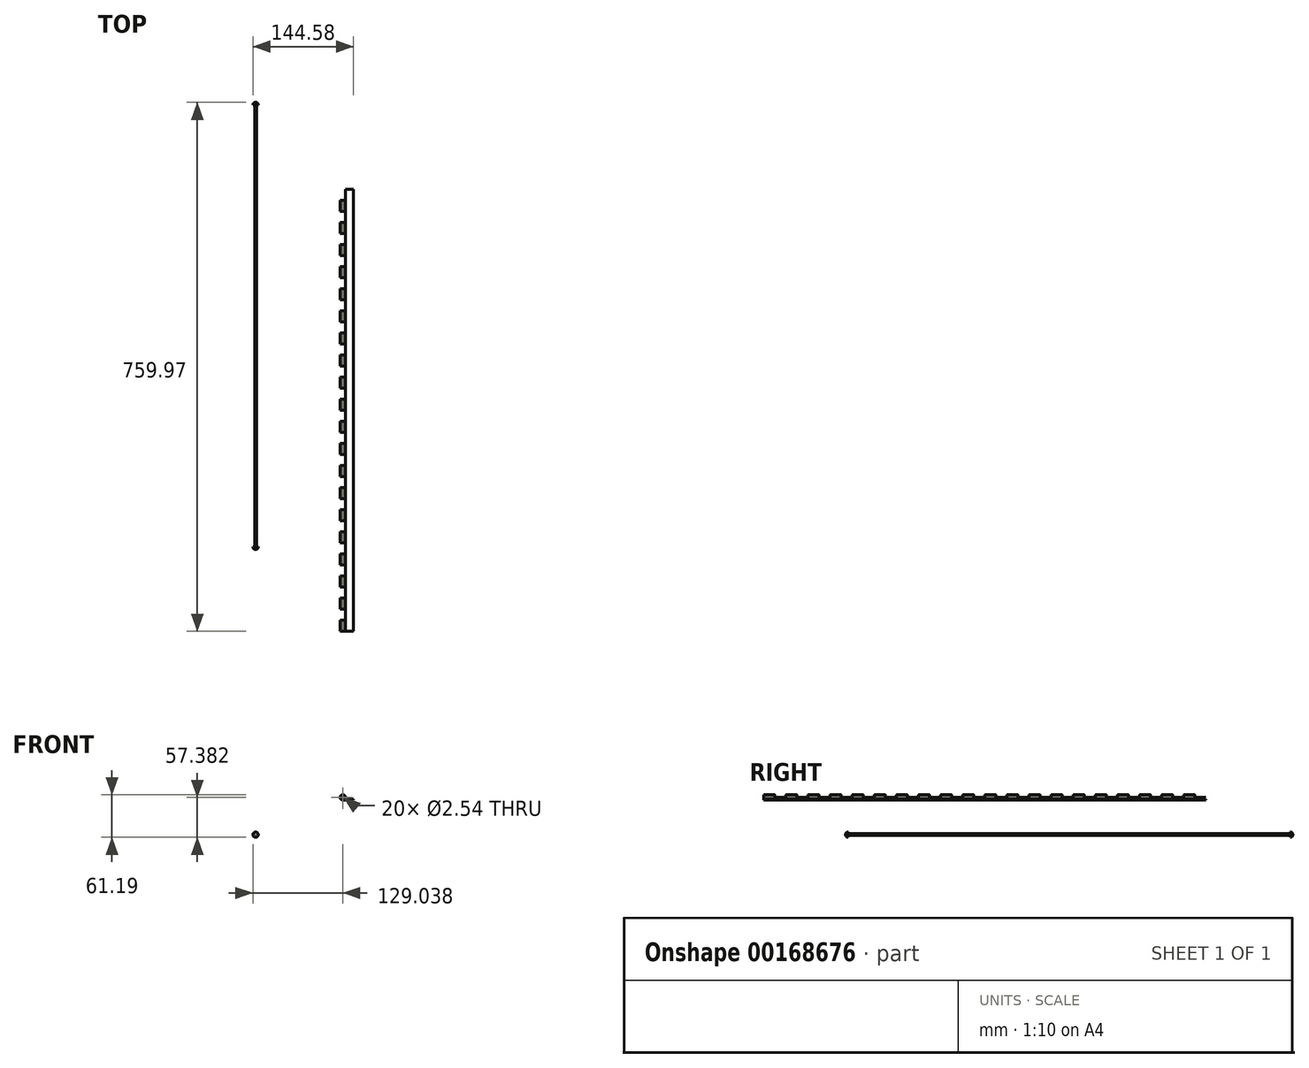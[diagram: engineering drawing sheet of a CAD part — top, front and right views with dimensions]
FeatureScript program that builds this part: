
annotation { "Feature Type Name" : "Feature", "Feature Type Description" : "" }
export const myFeature = defineFeature(function(context is Context, id is Id, definition is map)
    precondition{}
    {
        {
            var Q0;
            Q0=qCreatedBy(makeId("Front.planeOp"),FACE);
            var sketch = newSketch(context, id + "F0", { "sketchPlane" : qUnion([Q0])});
            skCircle(sketch, "E0", {"center": v(-17.02, 53.57) * mm, "radius": 3.81 * mm});
            skLineSegment(sketch, "E1", {"start": v(-17.02, 53.57) * mm, "end": v(-17.02, 20.01) * mm, "construction": true});
            skLineSegment(sketch, "E2", {"start": v(-17.02, 49.76) * mm, "end": v(-1.48, 49.76) * mm});
            skLineSegment(sketch, "E3", {"start": v(-1.48, 49.76) * mm, "end": v(-1.48, 51.03) * mm});
            skLineSegment(sketch, "E4", {"start": v(-1.48, 51.03) * mm, "end": v(-14.18, 51.03) * mm});
            skCircle(sketch, "E5", {"center": v(-17.02, 53.57) * mm, "radius": 1.27 * mm});
            skLineSegment(sketch, "E6", {"start": v(-14.18, 51.03) * mm, "end": v(-14.18, 67.2) * mm, "construction": true});
            skLineSegment(sketch, "E7", {"start": v(-17.02, 53.57) * mm, "end": v(18.39, 53.57) * mm});
            skPoint(sketch, "E8", {"position": v(-13.21, 53.57) * mm});
            skSolve(sketch);
        }
        {
            var Q0;
            Q0 = qSketchRegion(id + "F0", true);
            extrude(context, id + "F1", {"entities" : qUnion([Q0]), "depth" : 635 * mm});
        }
        {
            var Q0;
            Q0=qCreatedBy(makeId("Top.planeOp"),FACE);
            var sketch = newSketch(context, id + "F2", { "sketchPlane" : qUnion([Q0])});
            skLineSegment(sketch, "E9.bottom", {"start": v(-25.92, 0) * mm, "end": v(-13.22, 0) * mm});
            skLineSegment(sketch, "E9.top", {"start": v(-25.92, -15.87) * mm, "end": v(-13.22, -15.87) * mm});
            skLineSegment(sketch, "E9.left", {"start": v(-25.92, 0) * mm, "end": v(-25.92, -15.87) * mm});
            skLineSegment(sketch, "E9.right", {"start": v(-13.22, 0) * mm, "end": v(-13.22, -15.87) * mm});
            skLineSegment(sketch, "E10.0.1.0", {"start": v(-25.92, -31.75) * mm, "end": v(-25.92, -47.62) * mm});
            skLineSegment(sketch, "E10.0.1.1", {"start": v(-25.92, -31.75) * mm, "end": v(-13.22, -31.75) * mm});
            skLineSegment(sketch, "E10.0.1.2", {"start": v(-25.92, -47.62) * mm, "end": v(-13.22, -47.62) * mm});
            skLineSegment(sketch, "E10.0.1.3", {"start": v(-13.22, -31.75) * mm, "end": v(-13.22, -47.62) * mm});
            skLineSegment(sketch, "E10.0.2.0", {"start": v(-25.92, -63.5) * mm, "end": v(-25.92, -79.37) * mm});
            skLineSegment(sketch, "E10.0.2.1", {"start": v(-25.92, -63.5) * mm, "end": v(-13.22, -63.5) * mm});
            skLineSegment(sketch, "E10.0.2.2", {"start": v(-25.92, -79.38) * mm, "end": v(-13.22, -79.38) * mm});
            skLineSegment(sketch, "E10.0.2.3", {"start": v(-13.22, -63.5) * mm, "end": v(-13.22, -79.37) * mm});
            skLineSegment(sketch, "E10.0.3.0", {"start": v(-25.92, -95.25) * mm, "end": v(-25.92, -111.12) * mm});
            skLineSegment(sketch, "E10.0.3.1", {"start": v(-25.92, -95.25) * mm, "end": v(-13.22, -95.25) * mm});
            skLineSegment(sketch, "E10.0.3.2", {"start": v(-25.92, -111.12) * mm, "end": v(-13.22, -111.12) * mm});
            skLineSegment(sketch, "E10.0.3.3", {"start": v(-13.22, -95.25) * mm, "end": v(-13.22, -111.12) * mm});
            skLineSegment(sketch, "E10.0.4.0", {"start": v(-25.92, -127) * mm, "end": v(-25.92, -142.87) * mm});
            skLineSegment(sketch, "E10.0.4.1", {"start": v(-25.92, -127) * mm, "end": v(-13.22, -127) * mm});
            skLineSegment(sketch, "E10.0.4.2", {"start": v(-25.92, -142.88) * mm, "end": v(-13.22, -142.88) * mm});
            skLineSegment(sketch, "E10.0.4.3", {"start": v(-13.22, -127) * mm, "end": v(-13.22, -142.87) * mm});
            skLineSegment(sketch, "E10.0.5.0", {"start": v(-25.92, -158.75) * mm, "end": v(-25.92, -174.62) * mm});
            skLineSegment(sketch, "E10.0.5.1", {"start": v(-25.92, -158.75) * mm, "end": v(-13.22, -158.75) * mm});
            skLineSegment(sketch, "E10.0.5.2", {"start": v(-25.92, -174.62) * mm, "end": v(-13.22, -174.62) * mm});
            skLineSegment(sketch, "E10.0.5.3", {"start": v(-13.22, -158.75) * mm, "end": v(-13.22, -174.62) * mm});
            skLineSegment(sketch, "E10.0.6.0", {"start": v(-25.92, -190.5) * mm, "end": v(-25.92, -206.37) * mm});
            skLineSegment(sketch, "E10.0.6.1", {"start": v(-25.92, -190.5) * mm, "end": v(-13.22, -190.5) * mm});
            skLineSegment(sketch, "E10.0.6.2", {"start": v(-25.92, -206.38) * mm, "end": v(-13.22, -206.38) * mm});
            skLineSegment(sketch, "E10.0.6.3", {"start": v(-13.22, -190.5) * mm, "end": v(-13.22, -206.37) * mm});
            skLineSegment(sketch, "E10.0.7.0", {"start": v(-25.92, -222.25) * mm, "end": v(-25.92, -238.12) * mm});
            skLineSegment(sketch, "E10.0.7.1", {"start": v(-25.92, -222.25) * mm, "end": v(-13.22, -222.25) * mm});
            skLineSegment(sketch, "E10.0.7.2", {"start": v(-25.92, -238.12) * mm, "end": v(-13.22, -238.12) * mm});
            skLineSegment(sketch, "E10.0.7.3", {"start": v(-13.22, -222.25) * mm, "end": v(-13.22, -238.12) * mm});
            skLineSegment(sketch, "E10.0.8.0", {"start": v(-25.92, -254) * mm, "end": v(-25.92, -269.87) * mm});
            skLineSegment(sketch, "E10.0.8.1", {"start": v(-25.92, -254) * mm, "end": v(-13.22, -254) * mm});
            skLineSegment(sketch, "E10.0.8.2", {"start": v(-25.92, -269.88) * mm, "end": v(-13.22, -269.88) * mm});
            skLineSegment(sketch, "E10.0.8.3", {"start": v(-13.22, -254) * mm, "end": v(-13.22, -269.87) * mm});
            skLineSegment(sketch, "E10.0.9.0", {"start": v(-25.92, -285.75) * mm, "end": v(-25.92, -301.62) * mm});
            skLineSegment(sketch, "E10.0.9.1", {"start": v(-25.92, -285.75) * mm, "end": v(-13.22, -285.75) * mm});
            skLineSegment(sketch, "E10.0.9.2", {"start": v(-25.92, -301.62) * mm, "end": v(-13.22, -301.62) * mm});
            skLineSegment(sketch, "E10.0.9.3", {"start": v(-13.22, -285.75) * mm, "end": v(-13.22, -301.62) * mm});
            skLineSegment(sketch, "E10.0.10.0", {"start": v(-25.92, -317.5) * mm, "end": v(-25.92, -333.37) * mm});
            skLineSegment(sketch, "E10.0.10.1", {"start": v(-25.92, -317.5) * mm, "end": v(-13.22, -317.5) * mm});
            skLineSegment(sketch, "E10.0.10.2", {"start": v(-25.92, -333.38) * mm, "end": v(-13.22, -333.38) * mm});
            skLineSegment(sketch, "E10.0.10.3", {"start": v(-13.22, -317.5) * mm, "end": v(-13.22, -333.37) * mm});
            skLineSegment(sketch, "E10.0.11.0", {"start": v(-25.92, -349.25) * mm, "end": v(-25.92, -365.12) * mm});
            skLineSegment(sketch, "E10.0.11.1", {"start": v(-25.92, -349.25) * mm, "end": v(-13.22, -349.25) * mm});
            skLineSegment(sketch, "E10.0.11.2", {"start": v(-25.92, -365.12) * mm, "end": v(-13.22, -365.12) * mm});
            skLineSegment(sketch, "E10.0.11.3", {"start": v(-13.22, -349.25) * mm, "end": v(-13.22, -365.12) * mm});
            skLineSegment(sketch, "E10.direction1", {"start": v(-25.92, -15.87) * mm, "end": v(102.36, -15.87) * mm, "construction": true});
            skLineSegment(sketch, "E10.direction2", {"start": v(-25.92, -15.88) * mm, "end": v(-25.92, -47.62) * mm, "construction": true});
            skLineSegment(sketch, "E11.0.0.12", {"start": v(-25.92, -381) * mm, "end": v(-25.92, -396.87) * mm});
            skLineSegment(sketch, "E11.3.0.12", {"start": v(-25.92, -381) * mm, "end": v(-13.22, -381) * mm});
            skLineSegment(sketch, "E11.6.0.12", {"start": v(-25.92, -396.88) * mm, "end": v(-13.22, -396.88) * mm});
            skLineSegment(sketch, "E11.9.0.12", {"start": v(-13.22, -381) * mm, "end": v(-13.22, -396.87) * mm});
            skLineSegment(sketch, "E12.0.0.13", {"start": v(-25.92, -412.75) * mm, "end": v(-25.92, -428.62) * mm});
            skLineSegment(sketch, "E12.3.0.13", {"start": v(-25.92, -412.75) * mm, "end": v(-13.22, -412.75) * mm});
            skLineSegment(sketch, "E12.6.0.13", {"start": v(-25.92, -428.62) * mm, "end": v(-13.22, -428.62) * mm});
            skLineSegment(sketch, "E12.9.0.13", {"start": v(-13.22, -412.75) * mm, "end": v(-13.22, -428.62) * mm});
            skLineSegment(sketch, "E12.0.0.14", {"start": v(-25.92, -444.5) * mm, "end": v(-25.92, -460.37) * mm});
            skLineSegment(sketch, "E12.3.0.14", {"start": v(-25.92, -444.5) * mm, "end": v(-13.22, -444.5) * mm});
            skLineSegment(sketch, "E12.6.0.14", {"start": v(-25.92, -460.38) * mm, "end": v(-13.22, -460.38) * mm});
            skLineSegment(sketch, "E12.9.0.14", {"start": v(-13.22, -444.5) * mm, "end": v(-13.22, -460.37) * mm});
            skLineSegment(sketch, "E12.0.0.15", {"start": v(-25.92, -476.25) * mm, "end": v(-25.92, -492.12) * mm});
            skLineSegment(sketch, "E12.3.0.15", {"start": v(-25.92, -476.25) * mm, "end": v(-13.22, -476.25) * mm});
            skLineSegment(sketch, "E12.6.0.15", {"start": v(-25.92, -492.12) * mm, "end": v(-13.22, -492.12) * mm});
            skLineSegment(sketch, "E12.9.0.15", {"start": v(-13.22, -476.25) * mm, "end": v(-13.22, -492.12) * mm});
            skLineSegment(sketch, "E12.0.0.16", {"start": v(-25.92, -508) * mm, "end": v(-25.92, -523.87) * mm});
            skLineSegment(sketch, "E12.3.0.16", {"start": v(-25.92, -508) * mm, "end": v(-13.22, -508) * mm});
            skLineSegment(sketch, "E12.6.0.16", {"start": v(-25.92, -523.88) * mm, "end": v(-13.22, -523.88) * mm});
            skLineSegment(sketch, "E12.9.0.16", {"start": v(-13.22, -508) * mm, "end": v(-13.22, -523.87) * mm});
            skLineSegment(sketch, "E12.0.0.17", {"start": v(-25.92, -539.75) * mm, "end": v(-25.92, -555.62) * mm});
            skLineSegment(sketch, "E12.3.0.17", {"start": v(-25.92, -539.75) * mm, "end": v(-13.22, -539.75) * mm});
            skLineSegment(sketch, "E12.6.0.17", {"start": v(-25.92, -555.62) * mm, "end": v(-13.22, -555.62) * mm});
            skLineSegment(sketch, "E12.9.0.17", {"start": v(-13.22, -539.75) * mm, "end": v(-13.22, -555.62) * mm});
            skLineSegment(sketch, "E12.0.0.18", {"start": v(-25.92, -571.5) * mm, "end": v(-25.92, -587.37) * mm});
            skLineSegment(sketch, "E12.3.0.18", {"start": v(-25.92, -571.5) * mm, "end": v(-13.22, -571.5) * mm});
            skLineSegment(sketch, "E12.6.0.18", {"start": v(-25.92, -587.38) * mm, "end": v(-13.22, -587.38) * mm});
            skLineSegment(sketch, "E12.9.0.18", {"start": v(-13.22, -571.5) * mm, "end": v(-13.22, -587.37) * mm});
            skLineSegment(sketch, "E12.0.0.19", {"start": v(-25.92, -603.25) * mm, "end": v(-25.92, -619.12) * mm});
            skLineSegment(sketch, "E12.3.0.19", {"start": v(-25.92, -603.25) * mm, "end": v(-13.22, -603.25) * mm});
            skLineSegment(sketch, "E12.6.0.19", {"start": v(-25.92, -619.12) * mm, "end": v(-13.22, -619.12) * mm});
            skLineSegment(sketch, "E12.9.0.19", {"start": v(-13.22, -603.25) * mm, "end": v(-13.22, -619.12) * mm});
            skSolve(sketch);
        }
        {
            var Q0;
            Q0 = qSketchRegion(id + "F2", true);
            extrude(context, id + "F3", {"entities" : qUnion([Q0]), "operationType" : NewBodyOperationType.REMOVE, "depth" : 127 * mm});
        }
        {
            var Q0;
            Q0=qCreatedBy(makeId("Top.planeOp"),FACE);
            var sketch = newSketch(context, id + "F4", { "sketchPlane" : qUnion([Q0])});
            skLineSegment(sketch, "E13", {"start": v(-142.25, 121.16) * mm, "end": v(-140.98, 121.16) * mm});
            skLineSegment(sketch, "E14", {"start": v(-140.98, 121.16) * mm, "end": v(-140.98, -513.84) * mm});
            skLineSegment(sketch, "E15", {"start": v(-140.98, -513.84) * mm, "end": v(-142.25, -513.84) * mm});
            skLineSegment(sketch, "E16", {"start": v(-142.25, -513.84) * mm, "end": v(-142.25, 121.16) * mm});
            skLineSegment(sketch, "E17", {"start": v(-140.98, -513.84) * mm, "end": v(-138.44, -513.84) * mm});
            skArc(sketch, "E18", {"start": v(-138.44, -513.84) * mm, "mid": v(-139.56, -516.54) * mm, "end": v(-142.25, -517.65) * mm});
            skLineSegment(sketch, "E19", {"start": v(-142.25, -513.84) * mm, "end": v(-142.25, -517.65) * mm});
            skLineSegment(sketch, "E20", {"start": v(-140.98, 121.16) * mm, "end": v(-138.44, 121.16) * mm});
            skArc(sketch, "E21", {"start": v(-138.44, 121.16) * mm, "mid": v(-139.56, 123.85) * mm, "end": v(-142.25, 124.97) * mm});
            skLineSegment(sketch, "E22", {"start": v(-142.25, 121.16) * mm, "end": v(-142.25, 124.97) * mm});
            skSolve(sketch);
        }
        {
            var Q0;
            Q0 = qSketchRegion(id + "F4", true);
            var Q1;
            Q1=sQuery(id+"F4.wireOp",EDGE,"E16");
            revolve(context, id + "F5", {"entities" : qUnion([Q0]), "axis" : qUnion([Q1]), "revolveType" : RevolveType.FULL});
        }
    });
